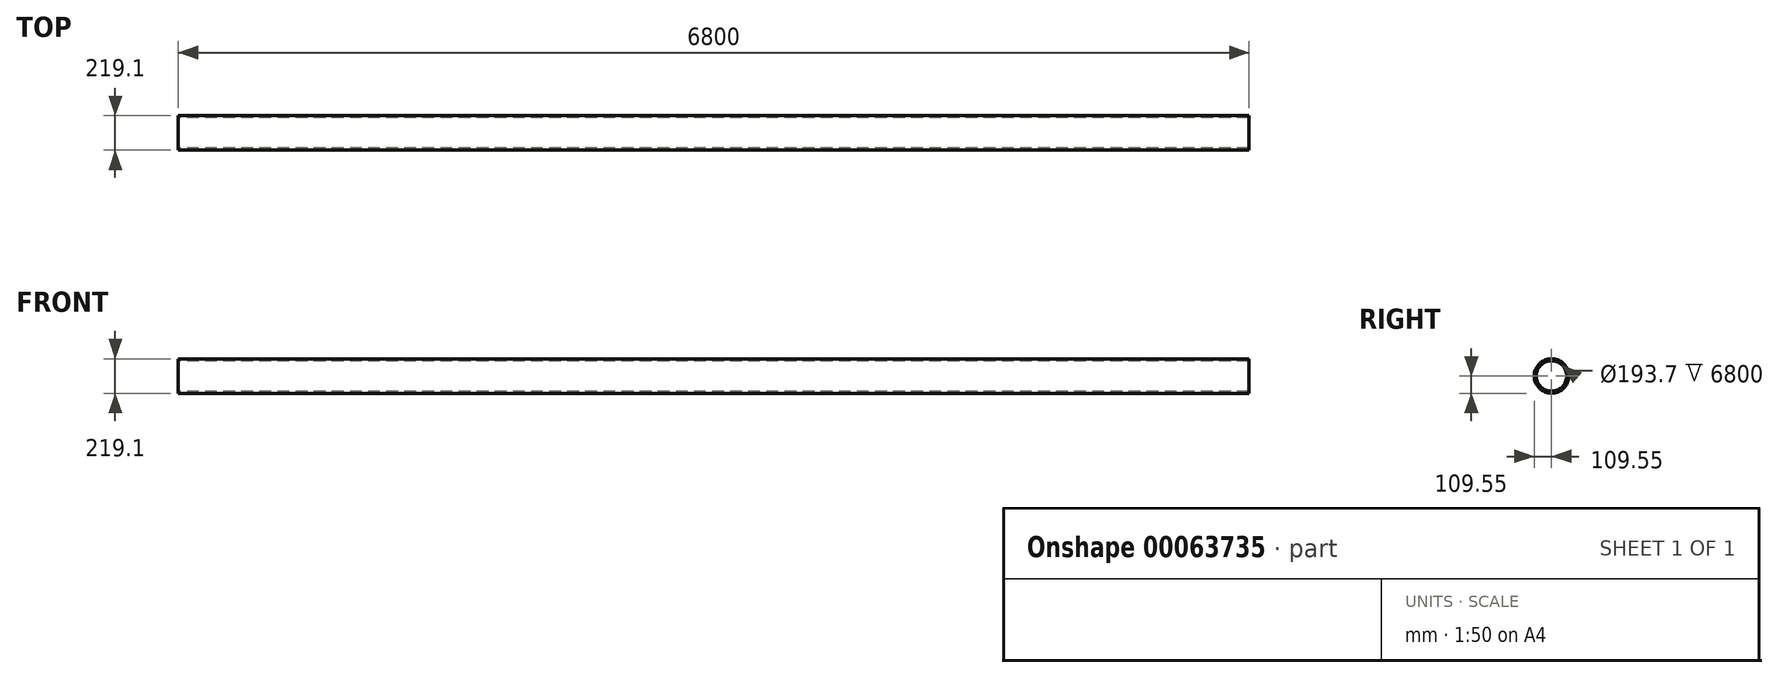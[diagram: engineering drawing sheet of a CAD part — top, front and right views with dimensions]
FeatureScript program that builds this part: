
annotation { "Feature Type Name" : "Feature", "Feature Type Description" : "" }
export const myFeature = defineFeature(function(context is Context, id is Id, definition is map)
    precondition{}
    {
        {
            var Q0;
            Q0=qCreatedBy(makeId("Right.planeOp"),FACE);
            var sketch = newSketch(context, id + "F0", { "sketchPlane" : qUnion([Q0])});
            skCircle(sketch, "E0", {"center": v(0, 0) * mm, "radius": 109.55 * mm});
            skCircle(sketch, "E1", {"center": v(0, 0) * mm, "radius": 96.85 * mm});
            skSolve(sketch);
        }
        {
            var Q0;
            Q0=makeQuery(id+"F0.imprint","IMPRINT",FACE,{"disambiguationData":[TD([[makeQuery(id+"F0.imprint","IMPRINT",EDGE,{"derivedFrom":sQuery(id+"F0.wireOp",EDGE,"E0")}),1.0]])]});
            extrude(context, id + "F1", {"entities" : qUnion([Q0]), "endBound" : BoundingType.SYMMETRIC, "depth" : 6800 * mm});
        }
    });
